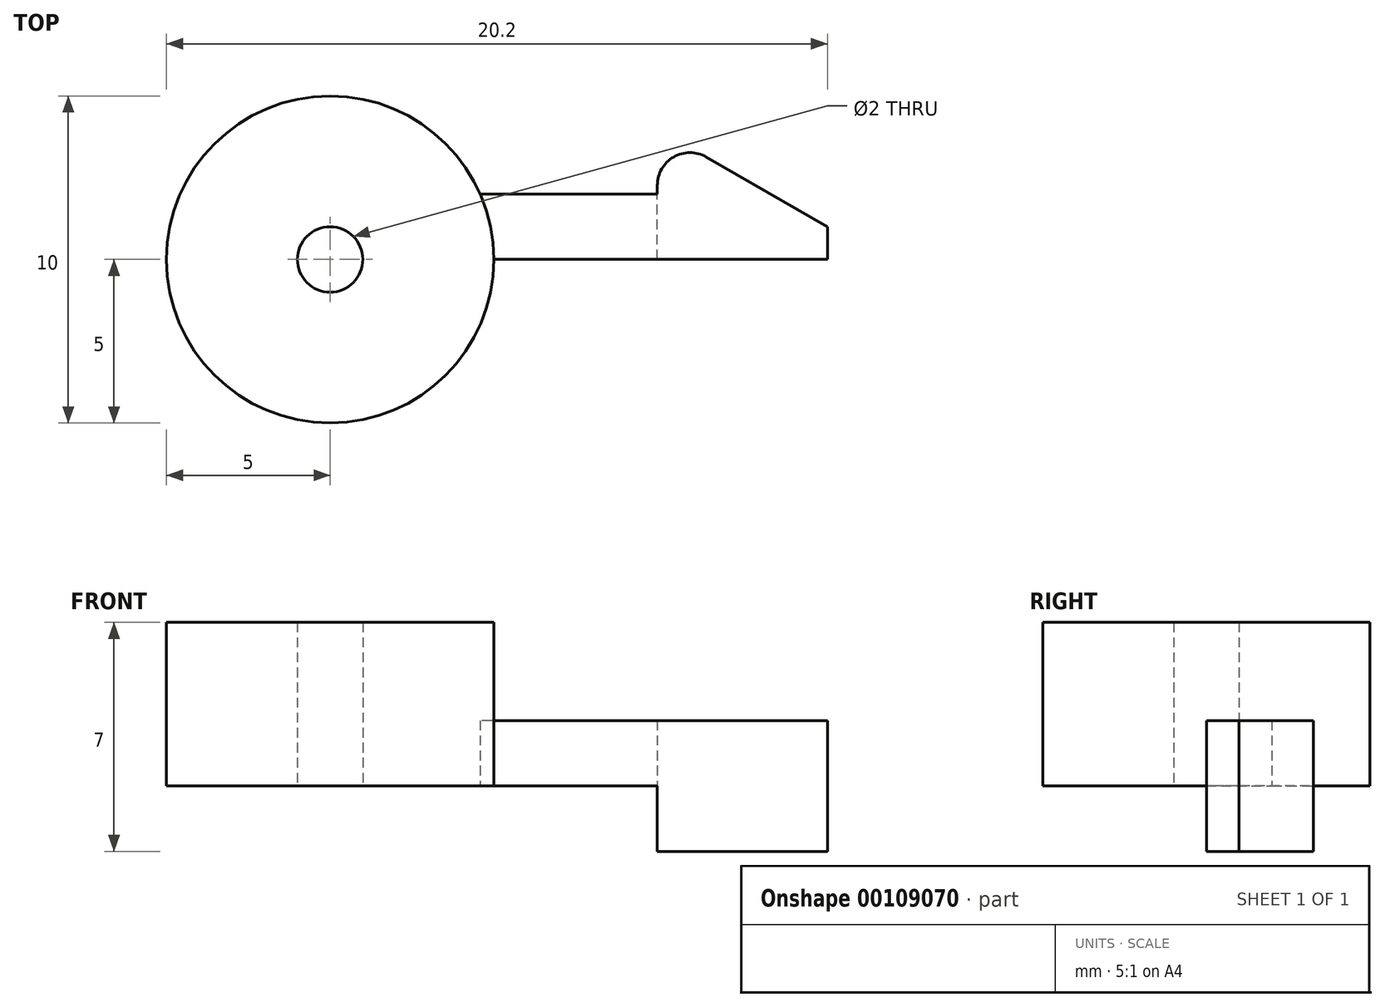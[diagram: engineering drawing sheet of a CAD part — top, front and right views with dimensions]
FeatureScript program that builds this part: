
annotation { "Feature Type Name" : "Feature", "Feature Type Description" : "" }
export const myFeature = defineFeature(function(context is Context, id is Id, definition is map)
    precondition{}
    {
        {
            var Q0;
            Q0=qCreatedBy(makeId("Top.planeOp"),FACE);
            var sketch = newSketch(context, id + "F0", { "sketchPlane" : qUnion([Q0])});
            skCircle(sketch, "E0", {"center": v(0, 0) * mm, "radius": 5 * mm});
            skLineSegment(sketch, "E1", {"start": v(5, 0) * mm, "end": v(10, 0) * mm});
            skLineSegment(sketch, "E2", {"start": v(10, 0) * mm, "end": v(10, 2) * mm});
            skLineSegment(sketch, "E3", {"start": v(10, 2) * mm, "end": v(4.58, 2) * mm});
            skLineSegment(sketch, "E4", {"start": v(10, 2) * mm, "end": v(10, 4) * mm});
            skLineSegment(sketch, "E5", {"start": v(10, 4) * mm, "end": v(15.2, 1) * mm});
            skLineSegment(sketch, "E6", {"start": v(15.2, 1) * mm, "end": v(15.2, 0) * mm});
            skLineSegment(sketch, "E7", {"start": v(15.2, 0) * mm, "end": v(10, 0) * mm});
            skSolve(sketch);
        }
        {
            var Q0;
            {var subQ0=sQuery(id+"F0.wireOp",EDGE,"E0");var subQ1=makeQuery(id+"F0.imprint","INTERSECT",VERTEX,{"derivedFrom":[subQ0,sQuery(id+"F0.wireOp",EDGE,"E1")]});Q0=makeQuery(id+"F0.imprint","IMPRINT",FACE,{"disambiguationData":[TD([[makeQuery(id+"F0.imprint","IMPRINT",EDGE,{"disambiguationData":[TD([[subQ1,-1.0]])],"derivedFrom":subQ0}),1.0]])]});}
            extrude(context, id + "F1", {"entities" : qUnion([Q0]), "depth" : 5 * mm});
        }
        {
            var Q0;
            {var subQ0=sQuery(id+"F0.wireOp",EDGE,"E1");Q0=makeQuery(id+"F0.imprint","IMPRINT",FACE,{"disambiguationData":[TD([[makeQuery(id+"F0.imprint","IMPRINT",EDGE,{"derivedFrom":subQ0}),1.0]])]});}
            extrude(context, id + "F2", {"entities" : qUnion([Q0]), "operationType" : NewBodyOperationType.ADD, "depth" : 2 * mm});
        }
        {
            var Q0;
            Q0=makeQuery(id+"F0.imprint","IMPRINT",FACE,{"disambiguationData":[TD([[makeQuery(id+"F0.imprint","IMPRINT",EDGE,{"derivedFrom":sQuery(id+"F0.wireOp",EDGE,"E2")}),-1.0]])]});
            extrude(context, id + "F3", {"entities" : qUnion([Q0]), "operationType" : NewBodyOperationType.ADD, "endBound" : BoundingType.SYMMETRIC, "depth" : 4 * mm});
        }
        {
            var Q0;
            Q0=makeQuery(id+"F3.opExtrude","SWEPT_EDGE",EDGE,{"disambiguationData":[OSD([sQuery(id+"F0.wireOp",EDGE,"E4"),sQuery(id+"F0.wireOp",EDGE,"E5")])]});
            fillet(context, id + "F4", {"entities" : qUnion([Q0]), "radius" : 1 * mm, "tangentPropagation" : true, "allowEdgeOverflow" : false});
        }
        {
            var Q0;
            Q0=sQuery(id+"F0.wireOp",VERTEX,"E0.center");
            var Q1;
            Q1=makeQuery(id+"F1.opExtrude","SWEPT_BODY",BODY,{"disambiguationData":[OSD([sQuery(id+"F0.wireOp",EDGE,"E0")])]});
            hole(context, id + "F5", {"style" : HoleStyle.SIMPLE, "endStyle" : HoleEndStyle.THROUGH, "oppositeDirection" : true, "holeDiameter" : 2 * mm, "locations" : qUnion([Q0]), "scope" : qUnion([Q1]), "isTappedThrough" : true});
        }
    });
